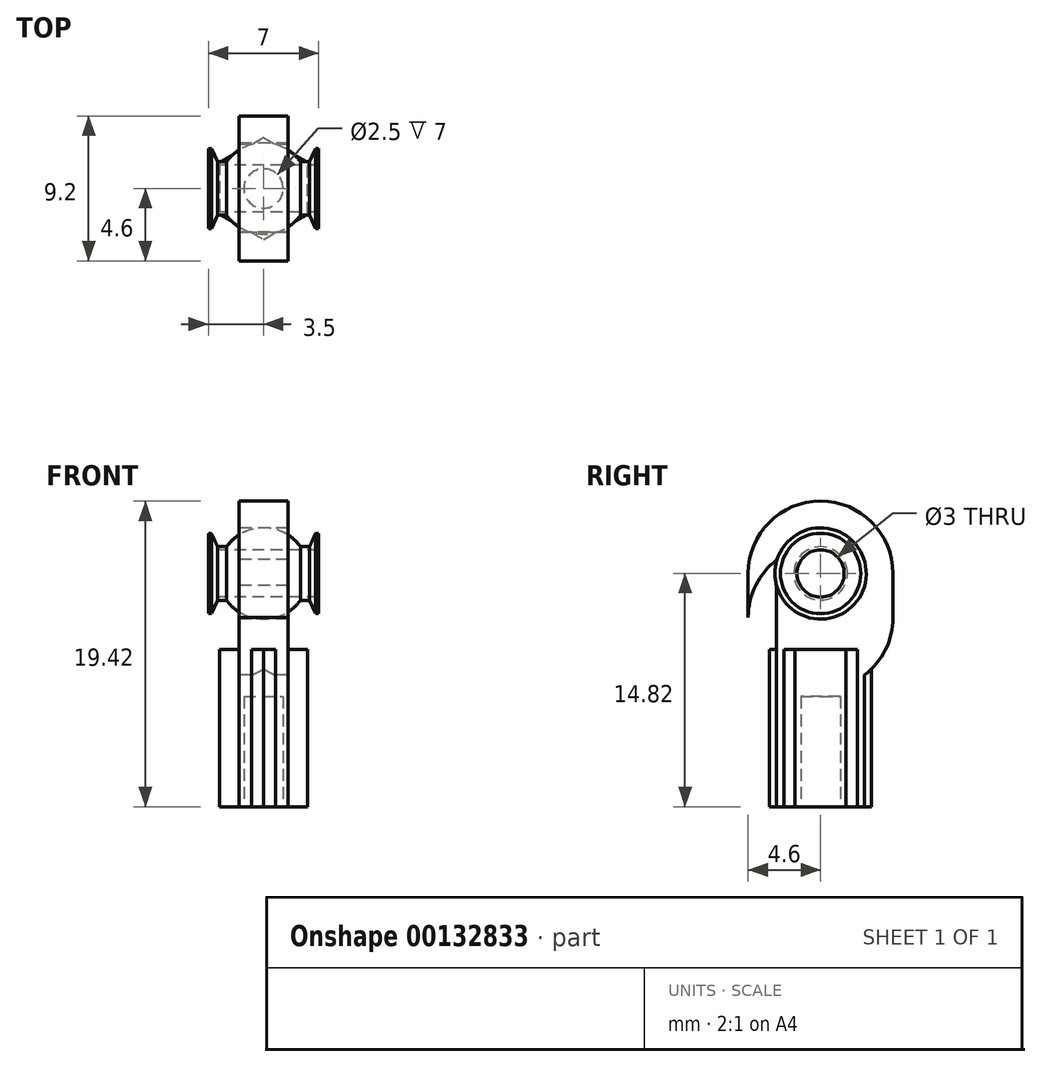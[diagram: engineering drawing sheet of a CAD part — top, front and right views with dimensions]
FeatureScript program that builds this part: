
annotation { "Feature Type Name" : "Feature", "Feature Type Description" : "" }
export const myFeature = defineFeature(function(context is Context, id is Id, definition is map)
    precondition{}
    {
        {
            var Q0;
            Q0=qCreatedBy(makeId("Front.planeOp"),FACE);
            var sketch = newSketch(context, id + "F0", { "sketchPlane" : qUnion([Q0])});
            skCircle(sketch, "E0", {"center": v(0, 0) * mm, "radius": 2.9 * mm});
            skLineSegment(sketch, "E1", {"start": v(3.5, 2.55) * mm, "end": v(3.5, -2.55) * mm});
            skLineSegment(sketch, "E2", {"start": v(0, 0) * mm, "end": v(3.5, 0) * mm, "construction": true});
            skLineSegment(sketch, "E3.0", {"start": v(3.3, 2.55) * mm, "end": v(3.3, -2.55) * mm, "construction": true});
            skLineSegment(sketch, "E4.MirrorCS", {"start": v(-3.5, 2.55) * mm, "end": v(-3.5, -2.55) * mm});
            skLineSegment(sketch, "E5.MirrorCS", {"start": v(-3.3, 2.55) * mm, "end": v(-3.3, -2.55) * mm, "construction": true});
            skLineSegment(sketch, "E6", {"start": v(-3.5, 1.5) * mm, "end": v(3.5, 1.5) * mm, "construction": true});
            skLineSegment(sketch, "E7.0", {"start": v(-3.5, 1.7) * mm, "end": v(3.5, 1.7) * mm, "construction": true});
            skLineSegment(sketch, "E8.MirrorCS", {"start": v(-3.5, -1.7) * mm, "end": v(3.5, -1.7) * mm, "construction": true});
            skLineSegment(sketch, "E9.MirrorCS", {"start": v(-3.5, -1.5) * mm, "end": v(3.5, -1.5) * mm, "construction": true});
            skLineSegment(sketch, "E10", {"start": v(3.5, 2.55) * mm, "end": v(3.3, 2.55) * mm});
            skLineSegment(sketch, "E11", {"start": v(3.3, 2.55) * mm, "end": v(2.93, 1.7) * mm});
            skLineSegment(sketch, "E12", {"start": v(2.93, 1.7) * mm, "end": v(2.35, 1.7) * mm});
            skLineSegment(sketch, "E13.MirrorCS", {"start": v(-3.5, 2.55) * mm, "end": v(-3.3, 2.55) * mm});
            skLineSegment(sketch, "E14.MirrorCS", {"start": v(-3.3, 2.55) * mm, "end": v(-2.93, 1.7) * mm});
            skLineSegment(sketch, "E15.MirrorCS", {"start": v(-2.93, 1.7) * mm, "end": v(-2.35, 1.7) * mm});
            skLineSegment(sketch, "E16.MirrorCS", {"start": v(-3.5, -2.55) * mm, "end": v(-3.3, -2.55) * mm});
            skLineSegment(sketch, "E17.MirrorCS", {"start": v(-3.3, -2.55) * mm, "end": v(-2.93, -1.7) * mm});
            skLineSegment(sketch, "E18.MirrorCS", {"start": v(-2.93, -1.7) * mm, "end": v(-2.35, -1.7) * mm});
            skLineSegment(sketch, "E19.MirrorCS", {"start": v(3.5, -2.55) * mm, "end": v(3.3, -2.55) * mm});
            skLineSegment(sketch, "E20.MirrorCS", {"start": v(3.3, -2.55) * mm, "end": v(2.93, -1.7) * mm});
            skLineSegment(sketch, "E21.MirrorCS", {"start": v(2.93, -1.7) * mm, "end": v(2.35, -1.7) * mm});
            skLineSegment(sketch, "E22", {"start": v(-6.75, 0) * mm, "end": v(5.98, 0) * mm});
            skSolve(sketch);
        }
        {
            var Q0;
            {var subQ0=sQuery(id+"F0.wireOp",EDGE,"E10");Q0=makeQuery(id+"F0.imprint","IMPRINT",FACE,{"disambiguationData":[TD([[makeQuery(id+"F0.imprint","IMPRINT",EDGE,{"derivedFrom":subQ0}),1.0]])]});}
            var Q1;
            {var subQ0=sQuery(id+"F0.wireOp",EDGE,"E0");var subQ1=makeQuery(id+"F0.imprint","INTERSECT",VERTEX,{"derivedFrom":[subQ0,sQuery(id+"F0.wireOp",EDGE,"E12")]});Q1=makeQuery(id+"F0.imprint","IMPRINT",FACE,{"disambiguationData":[TD([[makeQuery(id+"F0.imprint","IMPRINT",EDGE,{"disambiguationData":[TD([[subQ1,1.0]])],"derivedFrom":subQ0}),1.0]])]});}
            var Q2;
            {var subQ0=sQuery(id+"F0.wireOp",EDGE,"E13.MirrorCS");Q2=makeQuery(id+"F0.imprint","IMPRINT",FACE,{"disambiguationData":[TD([[makeQuery(id+"F0.imprint","IMPRINT",EDGE,{"derivedFrom":subQ0}),-1.0]])]});}
            var Q3;
            Q3=sQuery(id+"F0.wireOp",EDGE,"E2");
            revolve(context, id + "F1", {"entities" : qUnion([Q0, Q1, Q2]), "axis" : qUnion([Q3]), "revolveType" : RevolveType.FULL});
        }
        {
            var Q0;
            Q0=makeQuery(id+"F1.opRevolve","SWEPT_FACE",FACE,{"disambiguationData":[OSD([sQuery(id+"F0.wireOp",EDGE,"E4.MirrorCS")])]});
            var sketch = newSketch(context, id + "F2", { "sketchPlane" : qUnion([Q0])});
            skPoint(sketch, "E23.0", {"position": v(0, 1.5) * mm});
            skCircle(sketch, "E24", {"center": v(0, 0) * mm, "radius": 1.5 * mm});
            skSolve(sketch);
        }
        {
            var Q0;
            Q0=makeQuery(id+"F2.imprint","IMPRINT",FACE,{"disambiguationData":[TD([[makeQuery(id+"F2.imprint","IMPRINT",EDGE,{"derivedFrom":sQuery(id+"F2.wireOp",EDGE,"E24")}),1.0]])]});
            extrude(context, id + "F3", {"entities" : qUnion([Q0]), "operationType" : NewBodyOperationType.REMOVE, "endBound" : BoundingType.THROUGH_ALL, "oppositeDirection" : true, "depth" : 25 * mm});
        }
        {
            var Q0;
            Q0=qCreatedBy(makeId("Right.planeOp"),FACE);
            var sketch = newSketch(context, id + "F4", { "sketchPlane" : qUnion([Q0])});
            skCircle(sketch, "E25", {"center": v(0, 0) * mm, "radius": 4.6 * mm});
            skLineSegment(sketch, "E26", {"start": v(0, 2.9) * mm, "end": v(0, 0) * mm});
            skLineSegment(sketch, "E27", {"start": v(0, 0) * mm, "end": v(0, -2.9) * mm});
            skCircle(sketch, "E28", {"center": v(0, 0) * mm, "radius": 2.9 * mm});
            skLineSegment(sketch, "E29", {"start": v(-4.6, 0) * mm, "end": v(-4.6, -14.82) * mm});
            skLineSegment(sketch, "E30", {"start": v(-4.6, -14.82) * mm, "end": v(0, -14.82) * mm});
            skPoint(sketch, "E31", {"position": v(0, 4.6) * mm});
            skCircle(sketch, "E32", {"center": v(0, -2.8) * mm, "radius": 4.6 * mm});
            skLineSegment(sketch, "E33.MirrorCS", {"start": v(4.6, 0) * mm, "end": v(4.6, -14.82) * mm});
            skLineSegment(sketch, "E34.MirrorCS", {"start": v(4.6, -14.82) * mm, "end": v(0, -14.82) * mm});
            skLineSegment(sketch, "E35", {"start": v(-2.8, 0) * mm, "end": v(-2.8, -14.82) * mm});
            skLineSegment(sketch, "E36.MirrorCS", {"start": v(2.8, 0) * mm, "end": v(2.8, -14.82) * mm});
            skSolve(sketch);
        }
        {
            var Q0;
            {var subQ4=sQuery(id+"F4.wireOp",EDGE,"E25");var subQ7=makeQuery(id+"F4.imprint","INTERSECT",VERTEX,{"derivedFrom":[subQ4,sQuery(id+"F4.wireOp",EDGE,"E29")]});Q0=makeQuery(id+"F4.imprint","IMPRINT",FACE,{"disambiguationData":[TD([[makeQuery(id+"F4.imprint","IMPRINT",EDGE,{"disambiguationData":[TD([[subQ7,1.0]])],"derivedFrom":subQ4}),1.0]])]});}
            var Q1;
            {var subQ0=sQuery(id+"F4.wireOp",EDGE,"E32");var subQ1=sQuery(id+"F4.wireOp",EDGE,"E25");var subQ2=makeQuery(id+"F4.imprint","INTERSECT",VERTEX,{"disambiguationData":[OD(0.0)],"derivedFrom":[subQ1,subQ0]});Q1=makeQuery(id+"F4.imprint","IMPRINT",FACE,{"disambiguationData":[TD([[makeQuery(id+"F4.imprint","IMPRINT",EDGE,{"disambiguationData":[TD([[subQ2,-1.0]])],"derivedFrom":subQ1}),-1.0]])]});}
            var Q2;
            {var subQ0=sQuery(id+"F4.wireOp",EDGE,"E29");var subQ1=sQuery(id+"F4.wireOp",EDGE,"E25");var subQ2=makeQuery(id+"F4.imprint","INTERSECT",VERTEX,{"derivedFrom":[subQ1,subQ0]});Q2=makeQuery(id+"F4.imprint","IMPRINT",FACE,{"disambiguationData":[TD([[makeQuery(id+"F4.imprint","IMPRINT",EDGE,{"disambiguationData":[TD([[subQ2,-1.0]])],"derivedFrom":subQ1}),-1.0]])]});}
            var Q3;
            {var subQ0=sQuery(id+"F4.wireOp",EDGE,"E33.MirrorCS");var subQ1=sQuery(id+"F4.wireOp",EDGE,"E25");var subQ2=makeQuery(id+"F4.imprint","INTERSECT",VERTEX,{"derivedFrom":[subQ1,subQ0]});Q3=makeQuery(id+"F4.imprint","IMPRINT",FACE,{"disambiguationData":[TD([[makeQuery(id+"F4.imprint","IMPRINT",EDGE,{"disambiguationData":[TD([[subQ2,1.0]])],"derivedFrom":subQ1}),-1.0]])]});}
            var Q4;
            {var subQ2=sQuery(id+"F4.wireOp",EDGE,"E32");var subQ4=sQuery(id+"F4.wireOp",EDGE,"E25");var subQ7=makeQuery(id+"F4.imprint","INTERSECT",VERTEX,{"disambiguationData":[OD(0.0)],"derivedFrom":[subQ4,subQ2]});Q4=makeQuery(id+"F4.imprint","IMPRINT",FACE,{"disambiguationData":[TD([[makeQuery(id+"F4.imprint","IMPRINT",EDGE,{"disambiguationData":[TD([[subQ7,-1.0]])],"derivedFrom":subQ4}),1.0]])]});}
            var Q5;
            {var subQ0=sQuery(id+"F4.wireOp",EDGE,"E34.MirrorCS");var subQ1=sQuery(id+"F4.wireOp",EDGE,"E30");var subQ2=makeQuery(id+"F4.imprint","INTERSECT",VERTEX,{"derivedFrom":[subQ1,subQ0]});Q5=makeQuery(id+"F4.imprint","IMPRINT",FACE,{"disambiguationData":[TD([[makeQuery(id+"F4.imprint","IMPRINT",EDGE,{"disambiguationData":[TD([[subQ2,1.0]])],"derivedFrom":subQ1}),1.0]])]});}
            var Q6;
            {var subQ0=sQuery(id+"F4.wireOp",EDGE,"E35");var subQ1=sQuery(id+"F4.wireOp",EDGE,"E25");var subQ2=makeQuery(id+"F4.imprint","INTERSECT",VERTEX,{"derivedFrom":[subQ1,subQ0]});Q6=makeQuery(id+"F4.imprint","IMPRINT",FACE,{"disambiguationData":[TD([[makeQuery(id+"F4.imprint","IMPRINT",EDGE,{"disambiguationData":[TD([[subQ2,-1.0]])],"derivedFrom":subQ1}),-1.0]])]});}
            var Q7;
            {var subQ0=sQuery(id+"F4.wireOp",EDGE,"E35");var subQ3=sQuery(id+"F4.wireOp",EDGE,"E25");var subQ4=makeQuery(id+"F4.imprint","INTERSECT",VERTEX,{"derivedFrom":[subQ3,subQ0]});Q7=makeQuery(id+"F4.imprint","IMPRINT",FACE,{"disambiguationData":[TD([[makeQuery(id+"F4.imprint","IMPRINT",EDGE,{"disambiguationData":[TD([[subQ4,-1.0]])],"derivedFrom":subQ3}),1.0]])]});}
            var Q8;
            {var subQ0=sQuery(id+"F4.wireOp",EDGE,"E36.MirrorCS");var subQ1=sQuery(id+"F4.wireOp",EDGE,"E25");var subQ2=makeQuery(id+"F4.imprint","INTERSECT",VERTEX,{"derivedFrom":[subQ1,subQ0]});Q8=makeQuery(id+"F4.imprint","IMPRINT",FACE,{"disambiguationData":[TD([[makeQuery(id+"F4.imprint","IMPRINT",EDGE,{"disambiguationData":[TD([[subQ2,-1.0]])],"derivedFrom":subQ1}),-1.0]])]});}
            var Q9;
            {var subQ0=sQuery(id+"F4.wireOp",EDGE,"E36.MirrorCS");var subQ1=sQuery(id+"F4.wireOp",EDGE,"E25");var subQ2=makeQuery(id+"F4.imprint","INTERSECT",VERTEX,{"derivedFrom":[subQ1,subQ0]});Q9=makeQuery(id+"F4.imprint","IMPRINT",FACE,{"disambiguationData":[TD([[makeQuery(id+"F4.imprint","IMPRINT",EDGE,{"disambiguationData":[TD([[subQ2,-1.0]])],"derivedFrom":subQ1}),1.0]])]});}
            extrude(context, id + "F5", {"entities" : qUnion([Q0, Q1, Q2, Q3, Q4, Q5, Q6, Q7, Q8, Q9]), "endBound" : BoundingType.SYMMETRIC, "depth" : 3.1 * mm});
        }
        {
            var Q0;
            Q0=makeQuery(id+"F5.opExtrude","SWEPT_FACE",FACE,{"disambiguationData":[OSD([sQuery(id+"F4.wireOp",EDGE,"E30"),sQuery(id+"F4.wireOp",EDGE,"E34.MirrorCS")])]});
            var sketch = newSketch(context, id + "F6", { "sketchPlane" : qUnion([Q0])});
            skCircle(sketch, "E37.cCircle", {"center": v(0, 0) * mm, "radius": 2.8 * mm, "construction": true});
            skPoint(sketch, "E37.cCircle.perimeterSnap0", {"position": v(-1.55, 0) * mm});
            skLineSegment(sketch, "E37.0", {"start": v(-2.8, -1.62) * mm, "end": v(-2.8, 1.62) * mm});
            skLineSegment(sketch, "E37.1", {"start": v(-2.8, 1.62) * mm, "end": v(0, 3.23) * mm});
            skLineSegment(sketch, "E37.2", {"start": v(0, 3.23) * mm, "end": v(2.8, 1.62) * mm});
            skLineSegment(sketch, "E37.3", {"start": v(2.8, 1.62) * mm, "end": v(2.8, -1.62) * mm});
            skLineSegment(sketch, "E37.4", {"start": v(2.8, -1.62) * mm, "end": v(0, -3.23) * mm});
            skLineSegment(sketch, "E37.5", {"start": v(0, -3.23) * mm, "end": v(-2.8, -1.62) * mm});
            skPoint(sketch, "E37.0.midPoint", {"position": v(-2.8, 0) * mm});
            skPoint(sketch, "E37.0.midPoint.positionSnap0", {"position": v(-1.55, 0) * mm});
            skCircle(sketch, "E38", {"center": v(0, 0) * mm, "radius": 1.25 * mm});
            skSolve(sketch);
        }
        {
            var Q0;
            {var subQ0=sQuery(id+"F6.wireOp",EDGE,"E37.0");Q0=makeQuery(id+"F6.imprint","IMPRINT",FACE,{"disambiguationData":[TD([[makeQuery(id+"F6.imprint","IMPRINT",EDGE,{"derivedFrom":subQ0}),-1.0]])]});}
            var Q1;
            {var subQ7=sQuery(id+"F6.wireOp",EDGE,"E37.2");var subQ8=sQuery(id+"F6.wireOp",EDGE,"E37.1");var subQ9=makeQuery(id+"F6.imprint","INTERSECT",VERTEX,{"derivedFrom":[subQ8,subQ7]});Q1=makeQuery(id+"F6.imprint","IMPRINT",FACE,{"disambiguationData":[TD([[makeQuery(id+"F6.imprint","IMPRINT",EDGE,{"disambiguationData":[TD([[subQ9,1.0]])],"derivedFrom":subQ8}),-1.0]])]});}
            var Q2;
            {var subQ0=sQuery(id+"F6.wireOp",EDGE,"E37.3");Q2=makeQuery(id+"F6.imprint","IMPRINT",FACE,{"disambiguationData":[TD([[makeQuery(id+"F6.imprint","IMPRINT",EDGE,{"derivedFrom":subQ0}),-1.0]])]});}
            var Q3;
            {var subQ0=sQuery(id+"F6.wireOp",EDGE,"E37.5");var subQ1=sQuery(id+"F6.wireOp",EDGE,"E37.4");var subQ2=makeQuery(id+"F6.imprint","INTERSECT",VERTEX,{"derivedFrom":[subQ1,subQ0]});Q3=makeQuery(id+"F6.imprint","IMPRINT",FACE,{"disambiguationData":[TD([[makeQuery(id+"F6.imprint","IMPRINT",EDGE,{"disambiguationData":[TD([[subQ2,1.0]])],"derivedFrom":subQ1}),-1.0]])]});}
            var Q4;
            {var subQ0=sQuery(id+"F6.wireOp",EDGE,"E38");var subQ1=makeQuery(id+"F5.opExtrude","CAP_EDGE",EDGE,{"disambiguationData":[OSD([sQuery(id+"F4.wireOp",EDGE,"E30"),sQuery(id+"F4.wireOp",EDGE,"E34.MirrorCS")])],"isStart":true});var subQ2=makeQuery(id+"F6.imprint","INTERSECT",VERTEX,{"disambiguationData":[OD(0.0)],"derivedFrom":[subQ1,subQ0]});Q4=makeQuery(id+"F6.imprint","IMPRINT",FACE,{"disambiguationData":[TD([[makeQuery(id+"F6.imprint","IMPRINT",EDGE,{"disambiguationData":[TD([[subQ2,-1.0]])],"derivedFrom":subQ0}),1.0]])]});}
            var Q5;
            {var subQ0=sQuery(id+"F6.wireOp",EDGE,"E38");var subQ1=makeQuery(id+"F5.opExtrude","CAP_EDGE",EDGE,{"disambiguationData":[OSD([sQuery(id+"F4.wireOp",EDGE,"E30"),sQuery(id+"F4.wireOp",EDGE,"E34.MirrorCS")])],"isStart":false});var subQ2=makeQuery(id+"F6.imprint","INTERSECT",VERTEX,{"disambiguationData":[OD(0.0)],"derivedFrom":[subQ1,subQ0]});Q5=makeQuery(id+"F6.imprint","IMPRINT",FACE,{"disambiguationData":[TD([[makeQuery(id+"F6.imprint","IMPRINT",EDGE,{"disambiguationData":[TD([[subQ2,1.0]])],"derivedFrom":subQ0}),1.0]])]});}
            extrude(context, id + "F7", {"entities" : qUnion([Q0, Q1, Q2, Q3, Q4, Q5]), "operationType" : NewBodyOperationType.ADD, "oppositeDirection" : true, "depth" : 10 * mm});
        }
        {
            var Q0;
            {var subQ0=sQuery(id+"F6.wireOp",EDGE,"E38");var subQ1=makeQuery(id+"F5.opExtrude","CAP_EDGE",EDGE,{"disambiguationData":[OSD([sQuery(id+"F4.wireOp",EDGE,"E30"),sQuery(id+"F4.wireOp",EDGE,"E34.MirrorCS")])],"isStart":false});var subQ2=makeQuery(id+"F6.imprint","INTERSECT",VERTEX,{"disambiguationData":[OD(0.0)],"derivedFrom":[subQ1,subQ0]});Q0=makeQuery(id+"F6.imprint","IMPRINT",FACE,{"disambiguationData":[TD([[makeQuery(id+"F6.imprint","IMPRINT",EDGE,{"disambiguationData":[TD([[subQ2,1.0]])],"derivedFrom":subQ0}),1.0]])]});}
            var Q1;
            {var subQ0=sQuery(id+"F6.wireOp",EDGE,"E38");var subQ1=sQuery(id+"F4.wireOp",EDGE,"E34.MirrorCS");var subQ2=sQuery(id+"F4.wireOp",EDGE,"E30");var subQ3=makeQuery(id+"F5.opExtrude","CAP_EDGE",EDGE,{"disambiguationData":[OSD([subQ2,subQ1])],"isStart":true});var subQ4=makeQuery(id+"F6.imprint","INTERSECT",VERTEX,{"disambiguationData":[OD(0.0)],"derivedFrom":[subQ3,subQ0]});Q1=makeQuery(id+"F6.imprint","IMPRINT",FACE,{"disambiguationData":[TD([[makeQuery(id+"F6.imprint","IMPRINT",EDGE,{"disambiguationData":[TD([[subQ4,1.0]])],"derivedFrom":subQ0}),1.0]])]});}
            var Q2;
            {var subQ0=sQuery(id+"F6.wireOp",EDGE,"E38");var subQ1=makeQuery(id+"F5.opExtrude","CAP_EDGE",EDGE,{"disambiguationData":[OSD([sQuery(id+"F4.wireOp",EDGE,"E30"),sQuery(id+"F4.wireOp",EDGE,"E34.MirrorCS")])],"isStart":true});var subQ2=makeQuery(id+"F6.imprint","INTERSECT",VERTEX,{"disambiguationData":[OD(0.0)],"derivedFrom":[subQ1,subQ0]});Q2=makeQuery(id+"F6.imprint","IMPRINT",FACE,{"disambiguationData":[TD([[makeQuery(id+"F6.imprint","IMPRINT",EDGE,{"disambiguationData":[TD([[subQ2,-1.0]])],"derivedFrom":subQ0}),1.0]])]});}
            extrude(context, id + "F8", {"entities" : qUnion([Q0, Q1, Q2]), "operationType" : NewBodyOperationType.REMOVE, "oppositeDirection" : true, "depth" : 7 * mm});
        }
        {
            var Q0;
            Q0=qCreatedBy(makeId("Front.planeOp"),FACE);
            var sketch = newSketch(context, id + "F9", { "sketchPlane" : qUnion([Q0])});
            skLineSegment(sketch, "E39.0", {"start": v(-3.5, 2.55) * mm, "end": v(-3.5, -2.55) * mm, "construction": true});
            skLineSegment(sketch, "E39.1", {"start": v(-3.5, 2.55) * mm, "end": v(-3.3, 2.55) * mm, "construction": true});
            skLineSegment(sketch, "E39.2", {"start": v(-3.3, 2.55) * mm, "end": v(-2.93, 1.7) * mm, "construction": true});
            skLineSegment(sketch, "E39.3", {"start": v(-2.93, 1.7) * mm, "end": v(-2.35, 1.7) * mm, "construction": true});
            skCircle(sketch, "E39.4", {"center": v(0, 0) * mm, "radius": 2.9 * mm, "construction": true});
            skLineSegment(sketch, "E39.5", {"start": v(2.93, 1.7) * mm, "end": v(2.35, 1.7) * mm, "construction": true});
            skLineSegment(sketch, "E39.6", {"start": v(3.3, 2.55) * mm, "end": v(2.93, 1.7) * mm, "construction": true});
            skLineSegment(sketch, "E39.7", {"start": v(3.5, 2.55) * mm, "end": v(3.3, 2.55) * mm, "construction": true});
            skLineSegment(sketch, "E39.8", {"start": v(3.5, 2.55) * mm, "end": v(3.5, -2.55) * mm, "construction": true});
            skLineSegment(sketch, "E39.9", {"start": v(3.5, -2.55) * mm, "end": v(3.3, -2.55) * mm, "construction": true});
            skLineSegment(sketch, "E39.10", {"start": v(3.3, -2.55) * mm, "end": v(2.93, -1.7) * mm, "construction": true});
            skLineSegment(sketch, "E39.11", {"start": v(2.93, -1.7) * mm, "end": v(2.35, -1.7) * mm, "construction": true});
            skLineSegment(sketch, "E39.12", {"start": v(-3.3, -2.55) * mm, "end": v(-2.93, -1.7) * mm, "construction": true});
            skLineSegment(sketch, "E39.13", {"start": v(-3.5, -2.55) * mm, "end": v(-3.3, -2.55) * mm, "construction": true});
            skLineSegment(sketch, "E40", {"start": v(-1.55, 4.6) * mm, "end": v(1.55, 4.6) * mm, "construction": true});
            skLineSegment(sketch, "E41.0", {"start": v(-2.8, -4.82) * mm, "end": v(-2.8, -14.82) * mm, "construction": true});
            skLineSegment(sketch, "E42.0", {"start": v(-2.8, -4.82) * mm, "end": v(-1.55, -4.82) * mm, "construction": true});
            skLineSegment(sketch, "E43.0", {"start": v(2.8, -4.82) * mm, "end": v(2.8, -14.82) * mm, "construction": true});
            skLineSegment(sketch, "E44.0", {"start": v(1.55, -4.82) * mm, "end": v(2.8, -4.82) * mm, "construction": true});
            skLineSegment(sketch, "E45.0", {"start": v(1.55, -2.8) * mm, "end": v(1.55, -6.45) * mm, "construction": true});
            skLineSegment(sketch, "E46.0", {"start": v(-1.55, -2.8) * mm, "end": v(-1.55, -6.45) * mm, "construction": true});
            skLineSegment(sketch, "E47.0", {"start": v(1.55, 0) * mm, "end": v(1.55, 4.6) * mm, "construction": true});
            skLineSegment(sketch, "E48.0", {"start": v(-1.55, 0) * mm, "end": v(-1.55, 4.6) * mm, "construction": true});
            skCircle(sketch, "E49", {"center": v(0, 0) * mm, "radius": 4.85 * mm, "construction": true});
            skCircle(sketch, "E50", {"center": v(0, 0) * mm, "radius": 1.55 * mm, "construction": true});
            skLineSegment(sketch, "E51", {"start": v(-2.85, 3.93) * mm, "end": v(-1.48, -0.46) * mm, "construction": true});
            skLineSegment(sketch, "E52", {"start": v(-1.44, 4.64) * mm, "end": v(0, 0) * mm, "construction": true});
            skLineSegment(sketch, "E53", {"start": v(0, 4.85) * mm, "end": v(0, 0) * mm, "construction": true});
            skLineSegment(sketch, "E54", {"start": v(-2.43, 4.2) * mm, "end": v(0, 0) * mm, "construction": true});
            skLineSegment(sketch, "E55", {"start": v(-3.77, 3.43) * mm, "end": v(-1.08, 4.98) * mm, "construction": true});
            skLineSegment(sketch, "E56", {"start": v(-3.77, 3.43) * mm, "end": v(-1.34, -0.78) * mm, "construction": true});
            skSolve(sketch);
        }
    });
